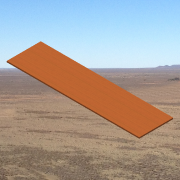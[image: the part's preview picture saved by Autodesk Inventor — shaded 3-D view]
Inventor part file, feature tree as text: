
AUTODESK INVENTOR PART (.ipt)
format: ipt  version: 2014 SP1 (Build 180222100, 222)  size: 124,416 bytes
history: native  units: in
note: dims shown in document units (in); Inventor stores cm internally (conversion verified against a paired STEP export)
features: extrude x1, sketch x1
ambient origin geometry x8: Origin, YZ Plane, XZ Plane, XY Plane, X Axis, Y Axis, Z Axis, Center Point
bodies: Solid1 (feature_tree)
feature tree (2):
  extrude  "Extrusion1"  Depth=20.0in
  sketch  "Sketch1"  dims[d0=78.0in d1=20.0in d2=0.75in d3=0.0in]
